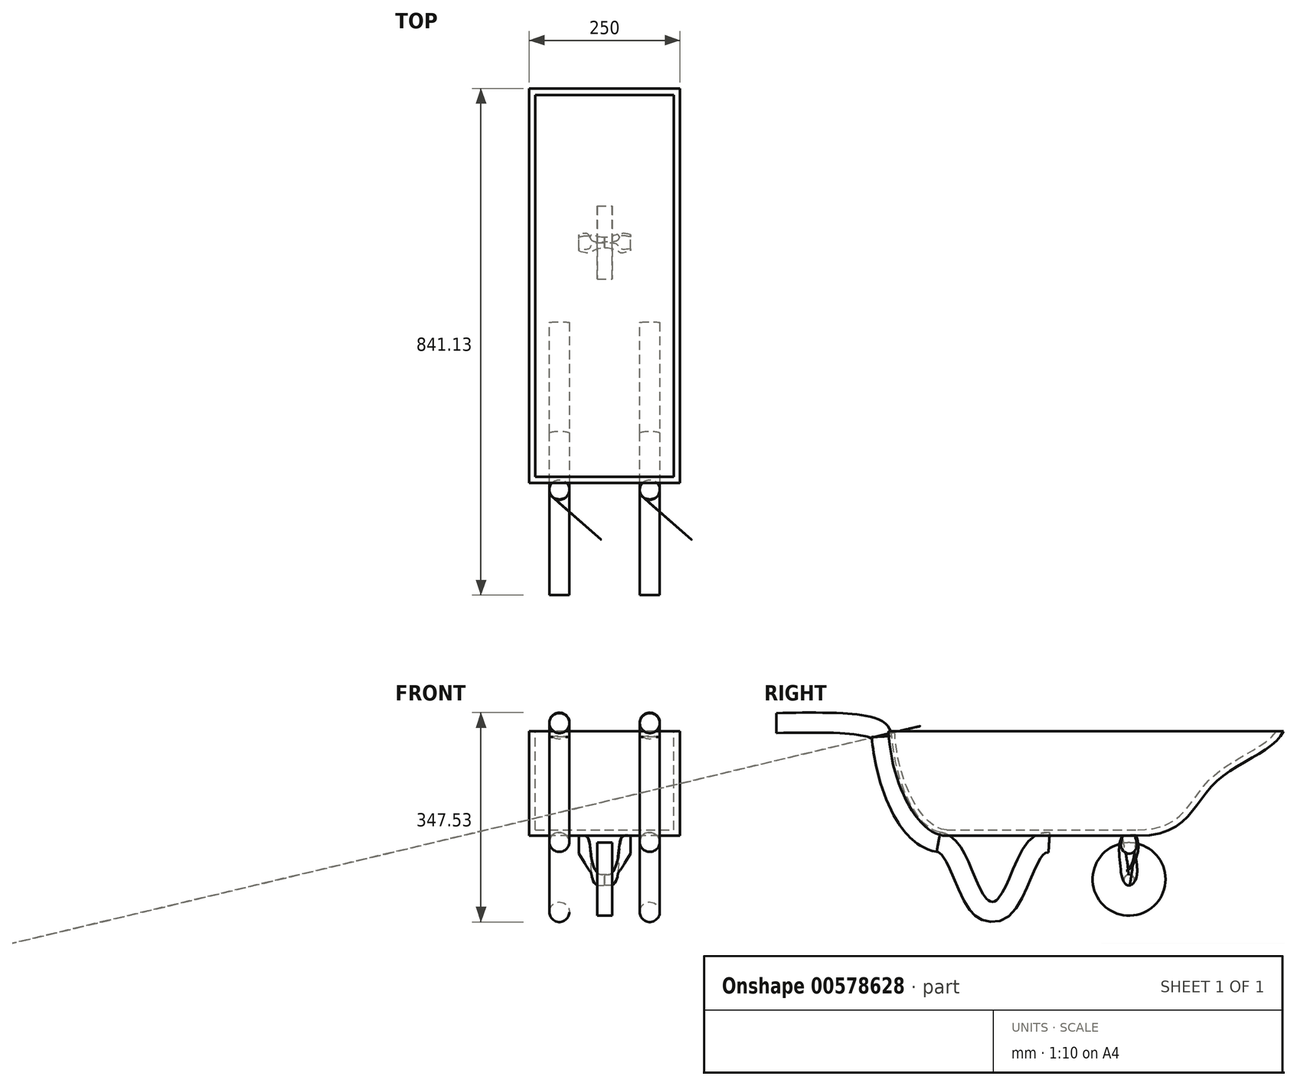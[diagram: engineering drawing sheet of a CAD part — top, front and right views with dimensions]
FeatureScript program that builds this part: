
annotation { "Feature Type Name" : "Feature", "Feature Type Description" : "" }
export const myFeature = defineFeature(function(context is Context, id is Id, definition is map)
    precondition{}
    {
        {
            var Q0;
            Q0=qCreatedBy(makeId("Right.planeOp"),FACE);
            var sketch = newSketch(context, id + "F0", { "sketchPlane" : qUnion([Q0])});
            skLineSegment(sketch, "E0", {"start": v(-222.78, -59.7) * mm, "end": v(94.02, -59.7) * mm});
            skFitSpline(sketch, "E1", {"points": [v(94.02, -59.7) * mm, v(223.9, 29.64) * mm, v(335.92, 114.16) * mm], "startDerivative": vector(493.7, 0) * mm, "endDerivative": vector(76.04, 196.8) * mm});
            skFitSpline(sketch, "E2", {"points": [v(-222.78, -59.7) * mm, v(-318.99, 114.16) * mm], "startDerivative": vector(-142.39, 0) * mm, "endDerivative": vector(-10.3, 261.82) * mm});
            skLineSegment(sketch, "E3", {"start": v(-318.99, 114.16) * mm, "end": v(335.92, 114.16) * mm});
            skSolve(sketch);
        }
        {
            var Q0;
            Q0 = qSketchRegion(id + "F0", true);
            extrude(context, id + "F1", {"entities" : qUnion([Q0]), "depth" : 250 * mm, "offsetDistance" : 25 * mm});
        }
        {
            var Q0;
            Q0=makeQuery(id+"F1.opExtrude","SWEPT_FACE",FACE,{"disambiguationData":[OSD([sQuery(id+"F0.wireOp",EDGE,"E3")])]});
            shell(context, id + "F2", {"entities" : qUnion([Q0]), "thickness" : 10 * mm});
        }
        {
            var Q0;
            Q0=qCreatedBy(makeId("Right.planeOp"),FACE);
            var sketch = newSketch(context, id + "F3", { "sketchPlane" : qUnion([Q0])});
            skFitSpline(sketch, "E4", {"points": [v(-320.32, 115.12) * mm, v(-226.27, -60) * mm], "startDerivative": vector(19.69, -239.1) * mm, "endDerivative": vector(158.31, -26.65) * mm});
            skFitSpline(sketch, "E5", {"points": [v(-226.27, -60) * mm, v(-199.67, -83.36) * mm, v(-162.7, -160.55) * mm, v(-136.76, -176.11) * mm, v(-112.1, -161.84) * mm, v(-74.49, -84) * mm, v(-42.7, -60.66) * mm], "startDerivative": vector(218.22, -36.73) * mm, "endDerivative": vector(296.58, -12.9) * mm});
            skFitSpline(sketch, "E6", {"points": [v(-320.32, 115.12) * mm, v(-339.02, 130.51) * mm, v(-495.2, 137.4) * mm], "startDerivative": vector(-6.2, 75.3) * mm, "endDerivative": vector(-272, -6.5) * mm});
            skLineSegment(sketch, "E7", {"start": v(-495.2, 137.4) * mm, "end": v(-495.2, 163.97) * mm});
            skSolve(sketch);
        }
        {
            var Q0;
            Q0=sQuery(id+"F3.wireOp",EDGE,"E7");
            cPlane(context, id + "F4", {"entities" : qUnion([Q0]), "cplaneType" : CPlaneType.LINE_ANGLE, "offset" : 25 * mm, "angle" : 90 * degree, "width" : 150 * mm, "height" : 150 * mm});
        }
        {
            var Q0;
            Q0=qCreatedBy(id+"F4.planeOp",FACE);
            var sketch = newSketch(context, id + "F5", { "sketchPlane" : qUnion([Q0])});
            skCircle(sketch, "E8", {"center": v(0, 137.42) * mm, "radius": 16.58 * mm});
            skSolve(sketch);
        }
        {
            var Q0;
            Q0=makeQuery(id+"F5.imprint","IMPRINT",FACE,{"disambiguationData":[TD([[makeQuery(id+"F5.imprint","IMPRINT",EDGE,{"derivedFrom":sQuery(id+"F5.wireOp",EDGE,"E8")}),1.0]])]});
            var Q1;
            Q1=sQuery(id+"F3.wireOp",EDGE,"E6");
            var Q2;
            Q2=sQuery(id+"F3.wireOp",EDGE,"E4");
            var Q3;
            Q3=sQuery(id+"F3.wireOp",EDGE,"E5");
            sweep(context, id + "F6", {"profiles" : qUnion([Q0]), "path" : qUnion([Q1, Q2, Q3])});
        }
        {
            var Q0;
            Q0=makeQuery(id+"F6.opSweep","SWEPT_BODY",BODY,{"disambiguationData":[OSD([sQuery(id+"F3.wireOp",EDGE,"E5"),sQuery(id+"F5.wireOp",EDGE,"E8")])]});
            transform(context, id + "F7", {"entities" : qUnion([Q0]), "transformType" : TransformType.COPY});
        }
        {
            var Q0;
            Q0=makeQuery(id+"F7.opPattern","COPY",BODY,{"derivedFrom":makeQuery(id+"F6.opSweep","SWEPT_BODY",BODY,{"disambiguationData":[OSD([sQuery(id+"F3.wireOp",EDGE,"E5"),sQuery(id+"F5.wireOp",EDGE,"E8")])]}),"instanceName":"1"});
            transform(context, id + "F8", {"entities" : qUnion([Q0]), "transformType" : TransformType.TRANSLATION_3D, "dx" : 200 * mm, "dy" : 0 * mm, "dz" : 0 * mm, "makeCopy" : false});
        }
        {
            var Q0;
            Q0=makeQuery(id+"F6.opSweep","SWEPT_BODY",BODY,{"disambiguationData":[OSD([sQuery(id+"F3.wireOp",EDGE,"E5"),sQuery(id+"F5.wireOp",EDGE,"E8")])]});
            transform(context, id + "F9", {"entities" : qUnion([Q0]), "transformType" : TransformType.TRANSLATION_3D, "dx" : 50 * mm, "dy" : 0 * mm, "dz" : 0 * mm, "makeCopy" : false});
        }
        {
            var Q0;
            Q0=makeQuery(id+"F6.opSweep","SWEPT_BODY",BODY,{"disambiguationData":[OSD([sQuery(id+"F3.wireOp",EDGE,"E5"),sQuery(id+"F5.wireOp",EDGE,"E8")])]});
            var Q1;
            Q1=makeQuery(id+"F7.opPattern","COPY",BODY,{"derivedFrom":makeQuery(id+"F6.opSweep","SWEPT_BODY",BODY,{"disambiguationData":[OSD([sQuery(id+"F3.wireOp",EDGE,"E5"),sQuery(id+"F5.wireOp",EDGE,"E8")])]}),"instanceName":"1"});
            transform(context, id + "F10", {"entities" : qUnion([Q0, Q1]), "transformType" : TransformType.TRANSLATION_3D, "dx" : 0 * mm, "dy" : -10 * mm, "dz" : -10 * mm, "makeCopy" : false});
        }
        {
            var Q0;
            Q0=qCreatedBy(makeId("Front.planeOp"),FACE);
            var sketch = newSketch(context, id + "F11", { "sketchPlane" : qUnion([Q0])});
            skLineSegment(sketch, "E9", {"start": v(156.32, -59.86) * mm, "end": v(156.32, -104.5) * mm});
            skLineSegment(sketch, "E10", {"start": v(133.84, -60.17) * mm, "end": v(133.84, -150.7) * mm});
            skLineSegment(sketch, "E11", {"start": v(144.43, -59.86) * mm, "end": v(144.43, -141.36) * mm});
            skLineSegment(sketch, "E12", {"start": v(167.78, -60.11) * mm, "end": v(167.78, -88.33) * mm});
            skLineSegment(sketch, "E13", {"start": v(125.11, -59.5) * mm, "end": v(125.11, -150.23) * mm});
            skSolve(sketch);
        }
        {
            var Q0;
            Q0=sQuery(id+"F11.wireOp",EDGE,"E10");
            cPlane(context, id + "F12", {"entities" : qUnion([Q0]), "cplaneType" : CPlaneType.LINE_ANGLE, "offset" : 25 * mm, "angle" : 0 * degree, "width" : 150 * mm, "height" : 150 * mm});
        }
        {
            var Q0;
            Q0=qCreatedBy(id+"F12.planeOp",FACE);
            var sketch = newSketch(context, id + "F13", { "sketchPlane" : qUnion([Q0])});
            skCircle(sketch, "E14", {"center": v(0, -132.75) * mm, "radius": 9.13 * mm});
            skSolve(sketch);
        }
        {
            var Q0;
            Q0=sQuery(id+"F11.wireOp",EDGE,"E9");
            cPlane(context, id + "F14", {"entities" : qUnion([Q0]), "cplaneType" : CPlaneType.LINE_ANGLE, "offset" : 25 * mm, "angle" : 0 * degree, "width" : 150 * mm, "height" : 150 * mm});
        }
        {
            var Q0;
            Q0=qCreatedBy(id+"F14.planeOp",FACE);
            var sketch = newSketch(context, id + "F15", { "sketchPlane" : qUnion([Q0])});
            skFitSpline(sketch, "E15", {"points": [v(11.56, -59.8) * mm, v(15.96, -84.1) * mm, v(0, -108.54) * mm, v(-14.88, -83.44) * mm, v(-11.28, -59.8) * mm], "startDerivative": vector(37.7, -90.35) * mm, "endDerivative": vector(32.01, 87.71) * mm});
            skLineSegment(sketch, "E16", {"start": v(11.56, -59.8) * mm, "end": v(-11.28, -59.8) * mm});
            skSolve(sketch);
        }
        {
            var Q0;
            Q0=sQuery(id+"F11.wireOp",EDGE,"E11");
            cPlane(context, id + "F16", {"entities" : qUnion([Q0]), "cplaneType" : CPlaneType.LINE_ANGLE, "offset" : 25 * mm, "angle" : 0 * degree, "width" : 150 * mm, "height" : 150 * mm});
        }
        {
            var Q0;
            Q0=qCreatedBy(id+"F16.planeOp",FACE);
            var sketch = newSketch(context, id + "F17", { "sketchPlane" : qUnion([Q0])});
            skCircle(sketch, "E17", {"center": v(0, -120.53) * mm, "radius": 13.28 * mm});
            skSolve(sketch);
        }
        {
            var Q0;
            Q0=sQuery(id+"F11.wireOp",EDGE,"E12");
            cPlane(context, id + "F18", {"entities" : qUnion([Q0]), "cplaneType" : CPlaneType.LINE_ANGLE, "offset" : 25 * mm, "angle" : 0 * degree, "width" : 150 * mm, "height" : 150 * mm});
        }
        {
            var Q0;
            Q0=qCreatedBy(id+"F18.planeOp",FACE);
            var sketch = newSketch(context, id + "F19", { "sketchPlane" : qUnion([Q0])});
            skFitSpline(sketch, "E18", {"points": [v(10.41, -59.56) * mm, v(12.96, -78.9) * mm, v(0, -89.52) * mm, v(-12.11, -79.75) * mm, v(-9.56, -59.56) * mm], "startDerivative": vector(26.43, -77.35) * mm, "endDerivative": vector(25.89, 79.18) * mm});
            skLineSegment(sketch, "E19", {"start": v(10.41, -59.56) * mm, "end": v(-9.56, -59.56) * mm});
            skSolve(sketch);
        }
        {
            var Q0;
            Q0=sQuery(id+"F11.wireOp",EDGE,"E13");
            cPlane(context, id + "F20", {"entities" : qUnion([Q0]), "cplaneType" : CPlaneType.LINE_ANGLE, "offset" : 25 * mm, "angle" : 0 * degree, "width" : 150 * mm, "height" : 150 * mm});
        }
        {
            var Q0;
            Q0=qCreatedBy(id+"F20.planeOp",FACE);
            var sketch = newSketch(context, id + "F21", { "sketchPlane" : qUnion([Q0])});
            skCircle(sketch, "E20", {"center": v(0, -132.76) * mm, "radius": 8.75 * mm});
            skSolve(sketch);
        }
        {
            var Q1;
            Q1=makeQuery(id+"F19.imprint","IMPRINT",FACE,{"disambiguationData":[TD([[makeQuery(id+"F19.imprint","IMPRINT",EDGE,{"derivedFrom":sQuery(id+"F19.wireOp",EDGE,"E18")}),-1.0]])]});
            var Q2;
            Q2=makeQuery(id+"F15.imprint","IMPRINT",FACE,{"disambiguationData":[TD([[makeQuery(id+"F15.imprint","IMPRINT",EDGE,{"derivedFrom":sQuery(id+"F15.wireOp",EDGE,"E15")}),-1.0]])]});
            var Q3;
            Q3=makeQuery(id+"F17.imprint","IMPRINT",FACE,{"disambiguationData":[TD([[makeQuery(id+"F17.imprint","IMPRINT",EDGE,{"derivedFrom":sQuery(id+"F17.wireOp",EDGE,"E17")}),1.0]])]});
            var Q4;
            Q4=makeQuery(id+"F13.imprint","IMPRINT",FACE,{"disambiguationData":[TD([[makeQuery(id+"F13.imprint","IMPRINT",EDGE,{"derivedFrom":sQuery(id+"F13.wireOp",EDGE,"E14")}),1.0]])]});
            var Q5;
            Q5=makeQuery(id+"F21.imprint","IMPRINT",FACE,{"disambiguationData":[TD([[makeQuery(id+"F21.imprint","IMPRINT",EDGE,{"derivedFrom":sQuery(id+"F21.wireOp",EDGE,"E20")}),1.0]])]});
            loft(context, id + "F22", {"sheetProfilesArray" : [{ "sheetProfileEntities" : qUnion([Q1]) }, { "sheetProfileEntities" : qUnion([Q2]) }, { "sheetProfileEntities" : qUnion([Q3]) }, { "sheetProfileEntities" : qUnion([Q4]) }, { "sheetProfileEntities" : qUnion([Q5]) }]});
        }
        {
            var Q0;
            Q0=makeQuery(id+"F22.opLoft","SWEPT_BODY",BODY,{"disambiguationData":[OSD([sQuery(id+"F13.wireOp",EDGE,"E14"),sQuery(id+"F15.wireOp",EDGE,"E15"),sQuery(id+"F17.wireOp",EDGE,"E17"),makeQuery(id+"F19.imprint","IMPRINT",FACE,{"disambiguationData":[TD([[makeQuery(id+"F19.imprint","IMPRINT",EDGE,{"derivedFrom":sQuery(id+"F19.wireOp",EDGE,"E18")}),-1.0]])]}),makeQuery(id+"F21.imprint","IMPRINT",FACE,{"disambiguationData":[TD([[makeQuery(id+"F21.imprint","IMPRINT",EDGE,{"derivedFrom":sQuery(id+"F21.wireOp",EDGE,"E20")}),1.0]])]})])]});
            var Q1;
            Q1=qCreatedBy(id+"F20.planeOp",FACE);
            mirror(context, id + "F23", {"entities" : qUnion([Q0]), "mirrorPlane" : qUnion([Q1])});
        }
        {
            var Q0;
            Q0=qCreatedBy(id+"F20.planeOp",FACE);
            var sketch = newSketch(context, id + "F24", { "sketchPlane" : qUnion([Q0])});
            skCircle(sketch, "E21", {"center": v(0, -131.66) * mm, "radius": 60.53 * mm});
            skSolve(sketch);
        }
        {
            var Q0;
            Q0=makeQuery(id+"F24.imprint","IMPRINT",FACE,{"disambiguationData":[TD([[makeQuery(id+"F24.imprint","IMPRINT",EDGE,{"derivedFrom":sQuery(id+"F24.wireOp",EDGE,"E21")}),1.0]])]});
            var Q1;
            Q1=sQuery(id+"F24.wireOp",EDGE,"E21");
            extrude(context, id + "F25", {"entities" : qUnion([Q0]), "surfaceEntities" : qUnion([Q1]), "depth" : 25 * mm, "offsetDistance" : 25 * mm});
        }
        {
            var Q0;
            Q0=makeQuery(id+"F25.opExtrude","SWEPT_BODY",BODY,{"disambiguationData":[OSD([sQuery(id+"F24.wireOp",EDGE,"E21")])]});
            transform(context, id + "F26", {"entities" : qUnion([Q0]), "transformType" : TransformType.TRANSLATION_3D, "dx" : 12.5 * mm, "dy" : 0 * mm, "dz" : 0 * mm, "makeCopy" : false});
        }
        {
            var Q0;
            Q0=makeQuery(id+"F22.opLoft","SWEPT_BODY",BODY,{"disambiguationData":[OSD([sQuery(id+"F13.wireOp",EDGE,"E14"),sQuery(id+"F15.wireOp",EDGE,"E15"),sQuery(id+"F17.wireOp",EDGE,"E17"),makeQuery(id+"F19.imprint","IMPRINT",FACE,{"disambiguationData":[TD([[makeQuery(id+"F19.imprint","IMPRINT",EDGE,{"derivedFrom":sQuery(id+"F19.wireOp",EDGE,"E18")}),-1.0]])]}),makeQuery(id+"F21.imprint","IMPRINT",FACE,{"disambiguationData":[TD([[makeQuery(id+"F21.imprint","IMPRINT",EDGE,{"derivedFrom":sQuery(id+"F21.wireOp",EDGE,"E20")}),1.0]])]})])]});
            var Q1;
            Q1=makeQuery(id+"F25.opExtrude","SWEPT_BODY",BODY,{"disambiguationData":[OSD([sQuery(id+"F24.wireOp",EDGE,"E21")])]});
            var Q2;
            Q2=makeQuery(id+"F23.opPattern","COPY",BODY,{"derivedFrom":makeQuery(id+"F22.opLoft","SWEPT_BODY",BODY,{"disambiguationData":[OSD([sQuery(id+"F13.wireOp",EDGE,"E14"),sQuery(id+"F15.wireOp",EDGE,"E15"),sQuery(id+"F17.wireOp",EDGE,"E17"),makeQuery(id+"F19.imprint","IMPRINT",FACE,{"disambiguationData":[TD([[makeQuery(id+"F19.imprint","IMPRINT",EDGE,{"derivedFrom":sQuery(id+"F19.wireOp",EDGE,"E18")}),-1.0]])]}),makeQuery(id+"F21.imprint","IMPRINT",FACE,{"disambiguationData":[TD([[makeQuery(id+"F21.imprint","IMPRINT",EDGE,{"derivedFrom":sQuery(id+"F21.wireOp",EDGE,"E20")}),1.0]])]})])]}),"instanceName":"1"});
            transform(context, id + "F27", {"entities" : qUnion([Q0, Q1, Q2]), "transformType" : TransformType.TRANSLATION_3D, "dx" : 0 * mm, "dy" : 80 * mm, "dz" : 0 * mm, "makeCopy" : false});
        }
    });
